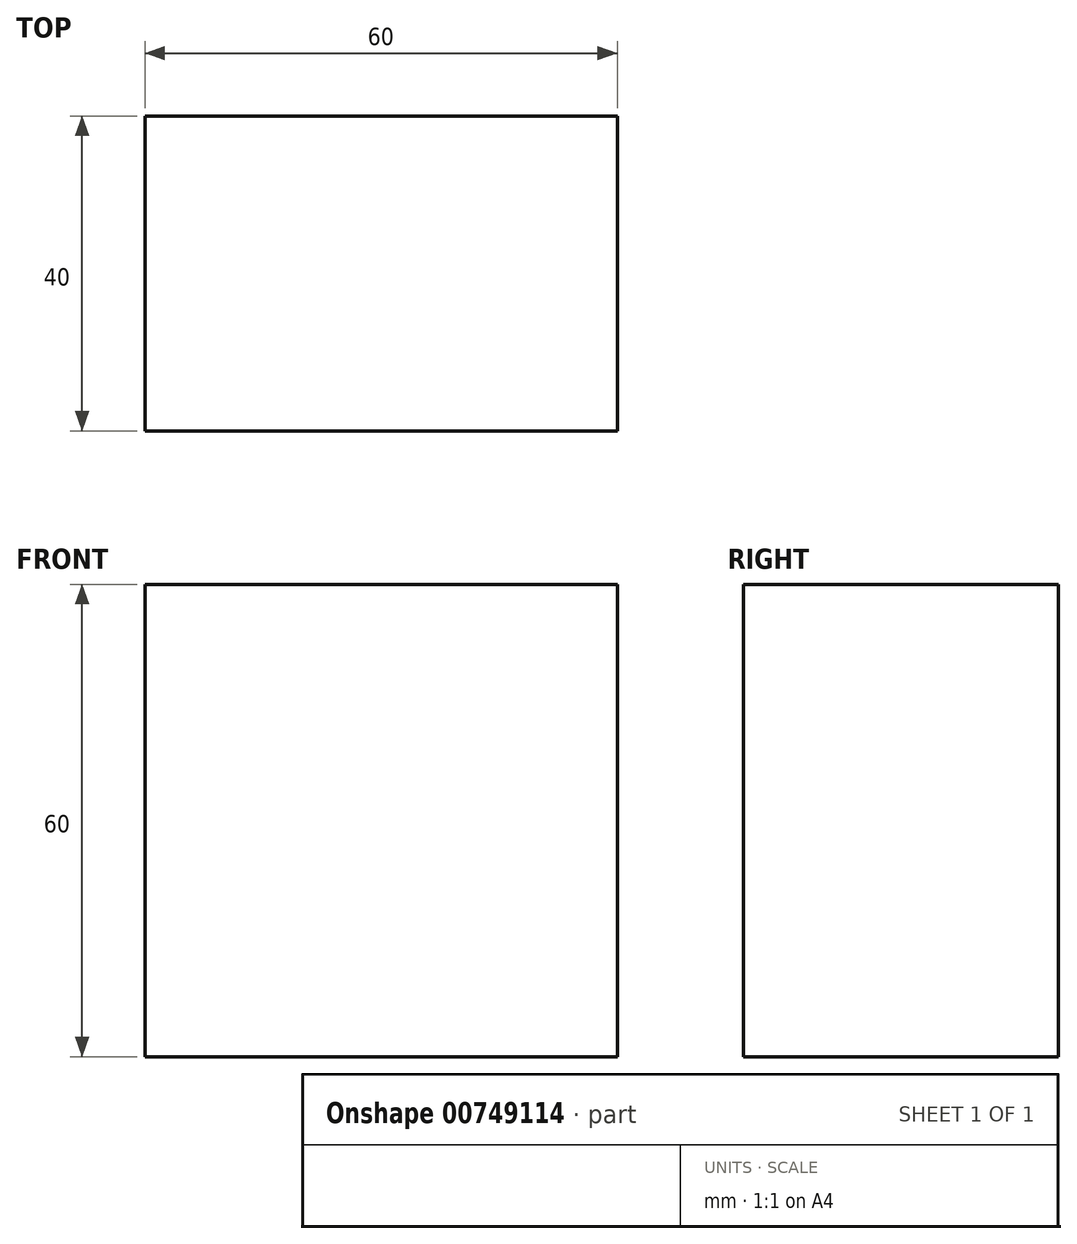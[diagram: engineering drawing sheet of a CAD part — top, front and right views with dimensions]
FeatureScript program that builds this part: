
annotation { "Feature Type Name" : "Feature", "Feature Type Description" : "" }
export const myFeature = defineFeature(function(context is Context, id is Id, definition is map)
    precondition{}
    {
        {
            var Q0;
            Q0=qCreatedBy(makeId("Front.planeOp"),FACE);
            var sketch = newSketch(context, id + "F0", { "sketchPlane" : qUnion([Q0])});
            skLineSegment(sketch, "E0", {"start": v(0, 0) * mm, "end": v(60, 0) * mm});
            skLineSegment(sketch, "E1", {"start": v(60, 0) * mm, "end": v(60, 60) * mm});
            skLineSegment(sketch, "E2", {"start": v(60, 60) * mm, "end": v(0, 60) * mm});
            skLineSegment(sketch, "E3", {"start": v(0, 60) * mm, "end": v(0, 0) * mm});
            skSolve(sketch);
        }
        {
            var Q0;
            Q0 = qSketchRegion(id + "F0", true);
            extrude(context, id + "F1", {"entities" : qUnion([Q0]), "depth" : 40 * mm, "offsetDistance" : 25 * mm});
        }
    });
